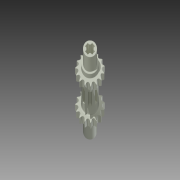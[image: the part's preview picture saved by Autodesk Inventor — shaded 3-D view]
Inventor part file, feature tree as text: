
AUTODESK INVENTOR PART (.ipt)
format: ipt  version: 2015 (Build 190159000, 159)  size: 694,784 bytes
history: native  units: mm
features: extrude x6, other x5, sketch x4, pattern_circular x2, imported_body x1, hole x1, projected_geometry x1
ambient origin geometry x8: Origin, YZ Plane, XZ Plane, XY Plane, X Axis, Y Axis, Z Axis, Center Point
bodies: Body1 (feature_tree)
feature tree (20):
  imported_body  "Base"
  extrude  "Tooth"  Depth=2.094395mm
  pattern_circular  "Teeth"  [2 undecoded]
  other  "Canal"
  extrude  "Axis"  Depth=4.0mm
  extrude  "Holes"  Depth=4.0mm
  sketch  "Boceto9"  dims[d18=2.094395mm]
  sketch  "Boceto10"  dims[d19=7.5mm]
  extrude  "Extrusión10"  Depth=4.0mm
  extrude  "Extrusión9"  Depth=4.0mm
  other  "EncoderPulse"
  pattern_circular  "Encoder"  [2 undecoded]
  extrude  "Extrusión11"  Depth=4.0mm TaperAngle=0.0deg
  other  "Tooth_drawing"
  other  "Canal_drawing"
  other  "Axis_drawing"
  hole  "Holes_drawing"  [1 undecoded]
  projected_geometry  "Contorno proyectado1"
  sketch  "Boceto8"  dims[d0=15.0mm d17=2.094395mm]
  sketch  "Boceto11"  dims[d20=1.5mm d21=2.248234mm d22=10.821041mm d23=10.821041mm d24=7.92mm d25=16.84218mm d26=7.92mm d35=15.0mm d36=0.0mm d37=150.0mm d38=360.0deg d48=5.0mm d50=12.474701mm d53=6.75mm d54=6.75mm d55=12.474701mm d56=6.75mm d57=4.678013mm d58=12.5mm d59=8.42109mm d60=5.0mm d61=15.0mm d62=90.0deg d63=0.5mm d64=4.0mm d65=1.6mm d66=10.0mm d67=0.0mm d68=1.5mm d69=60.0mm d71=360.0deg d73=10.0mm d74=0.0mm d75=5.0mm d76=7.0mm d77=22.5deg d78=80.0mm d79=360.0deg d81=8.0mm d82=28.0mm d83=0.0mm d84=10.0mm d85=18.0mm d86=0.0mm d87=4.5mm d88=3.0mm d90=12.0mm d91=0.0mm d94=2.0mm d95=2.0mm d96=5.5mm d97=5.5mm d98=0.1mm d99=4.0mm d100=0.1mm]
note: 5 required parameter values undecoded (feature->parameter linkage not recoverable at this tier; creation-order binding heuristic only, values carry confidence <= 0.55)
